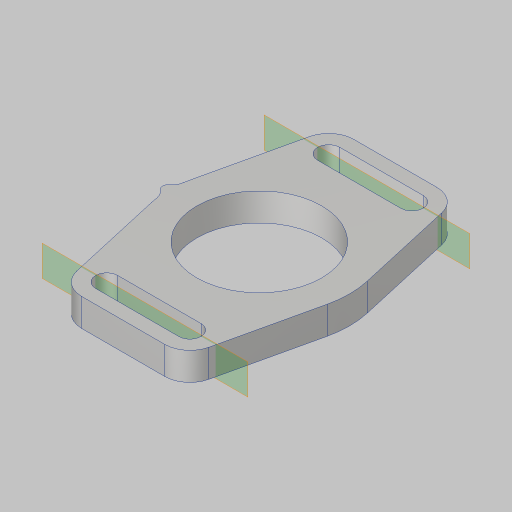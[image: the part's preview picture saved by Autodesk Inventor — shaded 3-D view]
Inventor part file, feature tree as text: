
AUTODESK INVENTOR PART (.ipt)
format: ipt  version: 2023.5 (Build 275446000, 446)  size: 172,032 bytes
history: native  units: in
note: dims shown in document units (in); Inventor stores cm internally (conversion verified against a paired STEP export)
features: sketch x2, extrude x2, plane x2, hole x1, fillet x1, projected_geometry x1
ambient origin geometry x8: Origin, YZ Plane, XZ Plane, XY Plane, X Axis, Y Axis, Z Axis, Center Point
bodies: Solid1 (feature_tree)
feature tree (9):
  sketch  "Sketch1"  dims[d0=1.125in d1=2.0in]
  extrude  "Extrusion1"  Depth=2.0in
  hole  "Hole1"  [1 undecoded]
  extrude  "Extrusion2"  Depth=0.125in
  fillet  "Fillet1"  Radius=0.25in
  plane  "Work Plane1"
  plane  "Work Plane2"
  sketch  "Sketch2"  dims[d2=1.432in d3=0.375in d4=0.375in d5=0.25in d6=0.25in d7=0.0in d8=0.201in d9=0.38in d10=0.385in d11=0.25in d12=0.5635in d13=1.0in d14=0.8108in d15=0.094in d16=0.825in d17=1.0in d18=0.0in d19=0.125in d20=0.201in d21=0.201in d22=0.75in d25=0.125in d26=0.125in]
  projected_geometry  "Project Cut Edges1"
note: 1 required parameter value undecoded (feature->parameter linkage not recoverable at this tier; creation-order binding heuristic only, values carry confidence <= 0.55)
